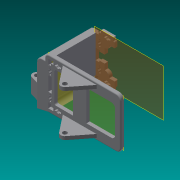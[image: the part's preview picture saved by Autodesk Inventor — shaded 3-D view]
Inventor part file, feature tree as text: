
AUTODESK INVENTOR PART (.ipt)
format: ipt  version: 2013 SP2 (Build 170200200, 200)  size: 1,046,016 bytes
history: native  units: in
note: dims shown in document units (in); Inventor stores cm internally (conversion verified against a paired STEP export)
features: extrude x25, fillet x21, sketch x21, reference x6, projected_geometry x4, plane x2
ambient origin geometry x8: Origin, YZ Plane, XZ Plane, XY Plane, X Axis, Y Axis, Z Axis, Center Point
bodies: Solid1 (feature_tree)
feature tree (79):
  plane  "Work Plane1"
  extrude  "Extrusion1"  Depth=0.125in
  fillet  "Fillet1"  Radius=0.4625in
  sketch  "Sketch2"  dims[d13=0.0in d14=0.925in]
  extrude  "Extrusion2"  Depth=0.925in
  extrude  "Extrusion3"  Depth=0.0938in TaperAngle=0.0deg
  extrude  "Extrusion4"  Depth=0.0938in TaperAngle=0.0deg
  extrude  "Extrusion5"  Depth=0.118in
  extrude  "Extrusion6"  Depth=0.118in
  extrude  "Extrusion7"  Depth=1.0in TaperAngle=0.0deg
  plane  "Work Plane2"
  extrude  "Extrusion9"  Depth=2.0in TaperAngle=0.0deg
  extrude  "Extrusion10"  Depth=2.3in TaperAngle=0.0deg
  extrude  "Extrusion11"  Depth=2.3in TaperAngle=0.0deg
  sketch  "Sketch8"  dims[d34=0.0938in d35=0.0in d36=1.0in d37=0.0in]
  extrude  "Extrusion12"  Depth=0.0938in TaperAngle=0.0deg
  extrude  "Extrusion13"  Depth=0.125in
  extrude  "Extrusion14"  Depth=0.125in
  extrude  "Extrusion15"  Depth=0.03in
  extrude  "Extrusion16"  Depth=0.03in
  extrude  "Extrusion17"  Depth=0.03in
  fillet  "Fillet2"  Radius=0.03in
  fillet  "Fillet3"  Radius=1.5in
  fillet  "Fillet4"  Radius=5.0in
  fillet  "Fillet5"  Radius=0.025in
  fillet  "Fillet6"  Radius=0.025in
  fillet  "Fillet7"  Radius=0.1in
  fillet  "Fillet8"  Radius=0.2in
  fillet  "Fillet9"  Radius=1.0in
  fillet  "Fillet10"  Radius=1.0in
  fillet  "Fillet11"  Radius=0.389in
  fillet  "Fillet12"  Radius=1.45in
  extrude  "Extrusion18"  Depth=0.01in
  extrude  "Extrusion19"  Depth=0.05in
  fillet  "Fillet13"  Radius=0.05in
  fillet  "Fillet14"  Radius=0.005in
  extrude  "Extrusion20"  Depth=0.1713in TaperAngle=0.0deg
  extrude  "Extrusion21"  [1 undecoded]
  extrude  "Extrusion22"  [1 undecoded]
  extrude  "Extrusion23"  [1 undecoded]
  extrude  "Extrusion24"  [1 undecoded]
  fillet  "Fillet15"  [1 undecoded]
  fillet  "Fillet16"  [1 undecoded]
  fillet  "Fillet17"  [1 undecoded]
  fillet  "Fillet18"  [1 undecoded]
  fillet  "Fillet19"  [1 undecoded]
  fillet  "Fillet20"  [1 undecoded]
  fillet  "Fillet21"  [1 undecoded]
  extrude  "Extrusion25"  [1 undecoded]
  extrude  "Extrusion26"  [1 undecoded]
  sketch  "Sketch1"  dims[d4=0.0938in d5=0.0in d6=0.125in d12=0.4625in]
  reference  "Reference1"
  reference  "Reference2"
  reference  "Reference3"
  sketch  "Sketch3"  dims[d16=0.0938in d17=0.0in d18=0.0938in d19=0.0in]
  sketch  "Sketch4"  dims[d20=0.0938in d21=0.0in d22=0.0938in d23=0.0in]
  reference  "Reference4"
  reference  "Reference5"
  reference  "Reference6"
  sketch  "Sketch6"  dims[d24=0.52in d25=0.0in d27=0.118in]
  sketch  "Sketch7"  dims[d28=2.0in d29=0.0in d31=0.118in]
  projected_geometry  "Projected Loop1"
  sketch  "Sketch9"  dims[d38=1.0in d39=0.0in d40=2.0in d41=0.0in]
  sketch  "Sketch10"  dims[d42=2.0in d43=0.0in d44=2.3in d45=0.0in]
  sketch  "Sketch11"  dims[d46=0.2in d47=2.3in d48=0.0in]
  sketch  "Sketch12"  dims[d49=10.0in d50=0.0in d51=0.0938in d52=0.0in]
  projected_geometry  "Projected Loop2"
  sketch  "Sketch13"  dims[d53=0.125in d54=0.125in]
  projected_geometry  "Projected Loop3"
  sketch  "Sketch14"  dims[d55=0.125in d56=0.125in]
  sketch  "Sketch15"  dims[d57=0.03in d58=0.03in]
  sketch  "Sketch16"  dims[d59=0.03in d60=0.03in]
  sketch  "Sketch17"  dims[d61=0.03in d62=0.03in d63=0.03in d64=1.5in d65=0.0in d66=5.0in d67=0.0in d68=0.025in d69=0.025in d70=0.1in d71=0.0in d72=0.2in d74=1.0in d75=0.0in d78=1.0in d79=0.0in d80=0.389in d81=0.0in d82=1.45in d83=0.0in]
  sketch  "Sketch18"  dims[d84=0.025in d85=0.01in]
  sketch  "Sketch19"  dims[d86=0.025in d87=0.05in d88=0.05in d89=0.005in]
  sketch  "Sketch20"  dims[d90=0.005in d91=0.1713in d92=0.0in]
  projected_geometry  "Projected Loop4"
  sketch  "Sketch21"  dims[d93=0.125in d94=0.0in]
  sketch  "Sketch22"
note: 13 required parameter values undecoded (feature->parameter linkage not recoverable at this tier; creation-order binding heuristic only, values carry confidence <= 0.55)
